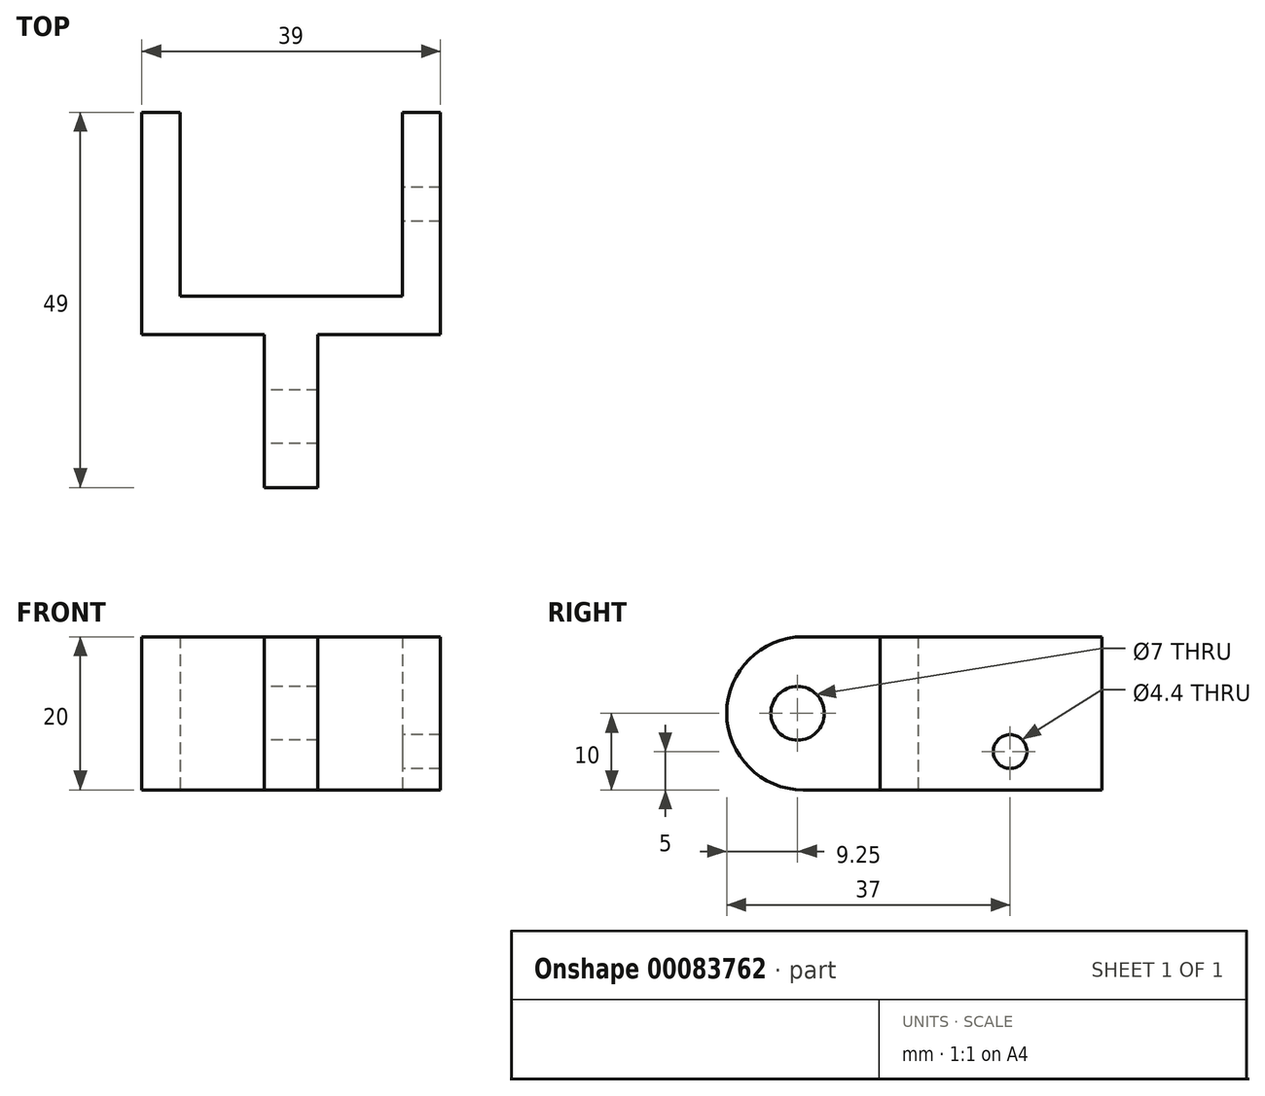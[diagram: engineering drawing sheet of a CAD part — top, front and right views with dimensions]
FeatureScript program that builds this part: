
annotation { "Feature Type Name" : "Feature", "Feature Type Description" : "" }
export const myFeature = defineFeature(function(context is Context, id is Id, definition is map)
    precondition{}
    {
        {
            var Q0;
            Q0=qCreatedBy(makeId("Top.planeOp"),FACE);
            var sketch = newSketch(context, id + "F0", { "sketchPlane" : qUnion([Q0])});
            skLineSegment(sketch, "E0", {"start": v(-23, 49) * mm, "end": v(-18, 49) * mm});
            skLineSegment(sketch, "E1", {"start": v(-18, 49) * mm, "end": v(-18, 25) * mm});
            skLineSegment(sketch, "E2", {"start": v(-18, 25) * mm, "end": v(11, 25) * mm});
            skLineSegment(sketch, "E3", {"start": v(11, 25) * mm, "end": v(11, 49) * mm});
            skLineSegment(sketch, "E4", {"start": v(11, 49) * mm, "end": v(16, 49) * mm});
            skLineSegment(sketch, "E5", {"start": v(16, 49) * mm, "end": v(16, 20) * mm});
            skLineSegment(sketch, "E6", {"start": v(16, 20) * mm, "end": v(0, 20) * mm});
            skLineSegment(sketch, "E7", {"start": v(0, 20) * mm, "end": v(0, 0) * mm});
            skLineSegment(sketch, "E8", {"start": v(0, 0) * mm, "end": v(-7, 0) * mm});
            skLineSegment(sketch, "E9", {"start": v(-7, 0) * mm, "end": v(-7, 20) * mm});
            skLineSegment(sketch, "E10", {"start": v(-7, 20) * mm, "end": v(-23, 20) * mm});
            skLineSegment(sketch, "E11", {"start": v(-23, 20) * mm, "end": v(-23, 49) * mm});
            skSolve(sketch);
        }
        {
            var Q0;
            Q0 = qSketchRegion(id + "F0", true);
            extrude(context, id + "F1", {"entities" : qUnion([Q0]), "depth" : 20 * mm});
        }
        {
            var Q0;
            Q0=makeQuery(id+"F1.opExtrude","CAP_EDGE",EDGE,{"disambiguationData":[OSD([sQuery(id+"F0.wireOp",EDGE,"E8")])],"isStart":false});
            var Q1;
            Q1=makeQuery(id+"F1.opExtrude","CAP_EDGE",EDGE,{"disambiguationData":[OSD([sQuery(id+"F0.wireOp",EDGE,"E8")])],"isStart":true});
            fillet(context, id + "F2", {"entities" : qUnion([Q0, Q1]), "radius" : 10 * mm, "tangentPropagation" : true, "allowEdgeOverflow" : false});
        }
        {
            var Q0;
            Q0=makeQuery(id+"F1.opExtrude","SWEPT_FACE",FACE,{"disambiguationData":[OSD([sQuery(id+"F0.wireOp",EDGE,"E5")])]});
            var sketch = newSketch(context, id + "F3", { "sketchPlane" : qUnion([Q0])});
            skPoint(sketch, "E12", {"position": v(37, 5) * mm});
            skPoint(sketch, "E13", {"position": v(9.25, 10) * mm});
            skPoint(sketch, "E14", {"position": v(20, 10) * mm});
            skSolve(sketch);
        }
        {
            var Q0;
            Q0=sQuery(id+"F3.wireOp",VERTEX,"E13");
            var Q1;
            Q1=makeQuery(id+"F1.opExtrude","SWEPT_BODY",BODY,{"disambiguationData":[OSD([sQuery(id+"F0.wireOp",EDGE,"E0"),sQuery(id+"F0.wireOp",EDGE,"E1"),sQuery(id+"F0.wireOp",EDGE,"E2"),sQuery(id+"F0.wireOp",EDGE,"E3"),sQuery(id+"F0.wireOp",EDGE,"E4"),sQuery(id+"F0.wireOp",EDGE,"E5"),sQuery(id+"F0.wireOp",EDGE,"E6"),sQuery(id+"F0.wireOp",EDGE,"E7"),sQuery(id+"F0.wireOp",EDGE,"E8"),sQuery(id+"F0.wireOp",EDGE,"E9"),sQuery(id+"F0.wireOp",EDGE,"E10"),sQuery(id+"F0.wireOp",EDGE,"E11")])]});
            hole(context, id + "F4", {"style" : HoleStyle.SIMPLE, "endStyle" : HoleEndStyle.THROUGH, "holeDiameter" : 7 * mm, "startFromSketch" : true, "locations" : qUnion([Q0]), "scope" : qUnion([Q1]), "isTappedThrough" : true});
        }
        {
            var Q0;
            Q0=sQuery(id+"F3.wireOp",VERTEX,"E12");
            var Q1;
            Q1=makeQuery(id+"F1.opExtrude","SWEPT_BODY",BODY,{"disambiguationData":[OSD([sQuery(id+"F0.wireOp",EDGE,"E0"),sQuery(id+"F0.wireOp",EDGE,"E1"),sQuery(id+"F0.wireOp",EDGE,"E2"),sQuery(id+"F0.wireOp",EDGE,"E3"),sQuery(id+"F0.wireOp",EDGE,"E4"),sQuery(id+"F0.wireOp",EDGE,"E5"),sQuery(id+"F0.wireOp",EDGE,"E6"),sQuery(id+"F0.wireOp",EDGE,"E7"),sQuery(id+"F0.wireOp",EDGE,"E8"),sQuery(id+"F0.wireOp",EDGE,"E9"),sQuery(id+"F0.wireOp",EDGE,"E10"),sQuery(id+"F0.wireOp",EDGE,"E11")])]});
            hole(context, id + "F5", {"style" : HoleStyle.SIMPLE, "endStyle" : HoleEndStyle.BLIND, "standardTappedOrClearance" : lookupTablePath({ "standard" : "ISO", "fit" : "Normal", "size" : "M4", "type" : "Clearance" }), "standardBlindInLast" : lookupTablePath({ "fit" : "Standard", "standard" : "ISO", "size" : "M4", "type" : "Clearance" }), "holeDiameter" : 4.4 * mm, "holeDepth" : 10 * mm, "startFromSketch" : true, "locations" : qUnion([Q0]), "scope" : qUnion([Q1])});
        }
    });
